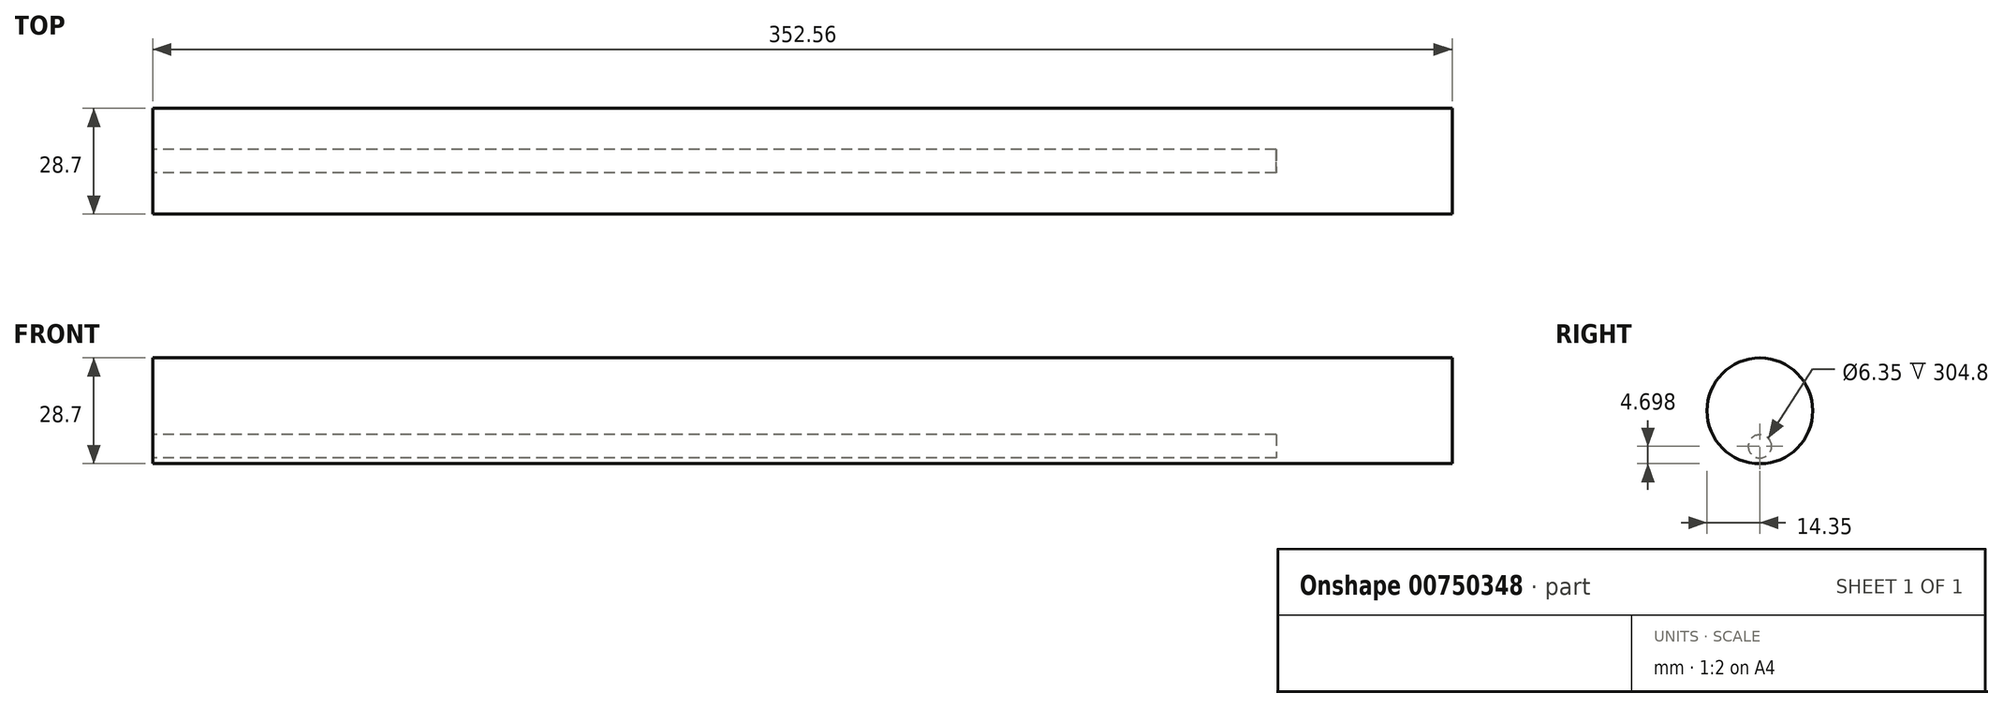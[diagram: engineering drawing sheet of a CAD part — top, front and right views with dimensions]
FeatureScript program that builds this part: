
annotation { "Feature Type Name" : "Feature", "Feature Type Description" : "" }
export const myFeature = defineFeature(function(context is Context, id is Id, definition is map)
    precondition{}
    {
        {
            var Q0;
            Q0=qCreatedBy(makeId("Right.planeOp"),FACE);
            var sketch = newSketch(context, id + "F0", { "sketchPlane" : qUnion([Q0])});
            skCircle(sketch, "E0", {"center": v(0, 0) * mm, "radius": 14.35 * mm});
            skSolve(sketch);
        }
        {
            var Q0;
            Q0 = qSketchRegion(id + "F0", true);
            extrude(context, id + "F1", {"entities" : qUnion([Q0]), "endBound" : BoundingType.SYMMETRIC, "depth" : 352.55 * mm, "offsetDistance" : 25.4 * mm});
        }
        {
            var Q0;
            Q0=makeQuery(id+"F1.opExtrude","CAP_FACE",FACE,{"disambiguationData":[OSD([sQuery(id+"F0.wireOp",EDGE,"E0")])],"isStart":true});
            var sketch = newSketch(context, id + "F2", { "sketchPlane" : qUnion([Q0])});
            skCircle(sketch, "E1", {"center": v(0, -9.65) * mm, "radius": 3.18 * mm});
            skSolve(sketch);
        }
        {
            var Q0;
            Q0 = qSketchRegion(id + "F2", true);
            extrude(context, id + "F3", {"entities" : qUnion([Q0]), "operationType" : NewBodyOperationType.REMOVE, "oppositeDirection" : true, "depth" : 304.8 * mm, "offsetDistance" : 25.4 * mm});
        }
    });
